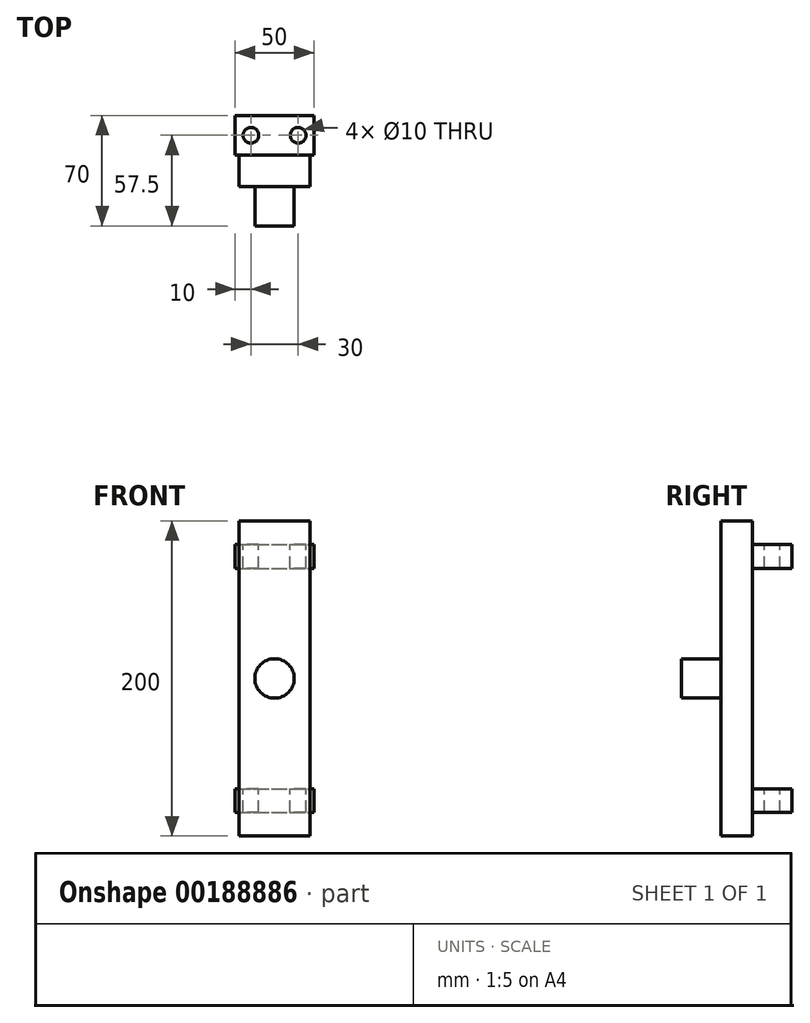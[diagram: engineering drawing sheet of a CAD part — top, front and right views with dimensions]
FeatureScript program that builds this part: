
annotation { "Feature Type Name" : "Feature", "Feature Type Description" : "" }
export const myFeature = defineFeature(function(context is Context, id is Id, definition is map)
    precondition{}
    {
        {
            var Q0;
            Q0=qCreatedBy(makeId("Front.planeOp"),FACE);
            var sketch = newSketch(context, id + "F0", { "sketchPlane" : qUnion([Q0])});
            skCircle(sketch, "E0", {"center": v(0, 0) * mm, "radius": 12.5 * mm});
            skSolve(sketch);
        }
        {
            var Q0;
            Q0 = qSketchRegion(id + "F0", true);
            extrude(context, id + "F1", {"entities" : qUnion([Q0]), "depth" : 45 * mm});
        }
        {
            var Q0;
            Q0=qCreatedBy(makeId("Front.planeOp"),FACE);
            cPlane(context, id + "F2", {"entities" : qUnion([Q0]), "cplaneType" : CPlaneType.OFFSET, "offset" : 20 * mm, "width" : 150 * mm, "height" : 150 * mm});
        }
        {
            var Q0;
            Q0=qCreatedBy(id+"F2.planeOp",FACE);
            var sketch = newSketch(context, id + "F3", { "sketchPlane" : qUnion([Q0])});
            skLineSegment(sketch, "E1.bottom", {"start": v(-22.5, -100) * mm, "end": v(22.5, -100) * mm});
            skLineSegment(sketch, "E1.top", {"start": v(-22.5, 100) * mm, "end": v(22.5, 100) * mm});
            skLineSegment(sketch, "E1.left", {"start": v(-22.5, -100) * mm, "end": v(-22.5, 100) * mm});
            skLineSegment(sketch, "E1.right", {"start": v(22.5, -100) * mm, "end": v(22.5, 100) * mm});
            skPoint(sketch, "E1.middle", {"position": v(0, 0) * mm});
            skSolve(sketch);
        }
        {
            var Q0;
            Q0 = qSketchRegion(id + "F3", true);
            extrude(context, id + "F4", {"entities" : qUnion([Q0]), "operationType" : NewBodyOperationType.ADD, "oppositeDirection" : true, "depth" : 20 * mm});
        }
        {
            var Q0;
            Q0=qCreatedBy(makeId("Front.planeOp"),FACE);
            cPlane(context, id + "F5", {"entities" : qUnion([Q0]), "cplaneType" : CPlaneType.OFFSET, "offset" : 25 * mm, "oppositeDirection" : true, "width" : 150 * mm, "height" : 150 * mm});
        }
        {
            var Q0;
            Q0=qCreatedBy(id+"F5.planeOp",FACE);
            var sketch = newSketch(context, id + "F6", { "sketchPlane" : qUnion([Q0])});
            skLineSegment(sketch, "E2.bottom", {"start": v(-25, 70) * mm, "end": v(25, 70) * mm});
            skLineSegment(sketch, "E2.top", {"start": v(-25, 85) * mm, "end": v(25, 85) * mm});
            skLineSegment(sketch, "E2.left", {"start": v(-25, 70) * mm, "end": v(-25, 85) * mm});
            skLineSegment(sketch, "E2.right", {"start": v(25, 70) * mm, "end": v(25, 85) * mm});
            skPoint(sketch, "E2.middle", {"position": v(0, 77.5) * mm});
            skLineSegment(sketch, "E3.bottom", {"start": v(-25, -85) * mm, "end": v(25, -85) * mm});
            skLineSegment(sketch, "E3.top", {"start": v(-25, -70) * mm, "end": v(25, -70) * mm});
            skLineSegment(sketch, "E3.left", {"start": v(-25, -85) * mm, "end": v(-25, -70) * mm});
            skLineSegment(sketch, "E3.right", {"start": v(25, -85) * mm, "end": v(25, -70) * mm});
            skPoint(sketch, "E3.middle", {"position": v(0, -77.5) * mm});
            skSolve(sketch);
        }
        {
            var Q0;
            Q0 = qSketchRegion(id + "F6", true);
            extrude(context, id + "F7", {"entities" : qUnion([Q0]), "operationType" : NewBodyOperationType.ADD, "depth" : 25 * mm});
        }
        {
            var Q0;
            Q0=makeQuery(id+"F7.opExtrude","SWEPT_FACE",FACE,{"disambiguationData":[OSD([sQuery(id+"F6.wireOp",EDGE,"E2.top")])]});
            var sketch = newSketch(context, id + "F8", { "sketchPlane" : qUnion([Q0])});
            skCircle(sketch, "E4", {"center": v(15, 12.5) * mm, "radius": 5 * mm});
            skCircle(sketch, "E5", {"center": v(-15, 12.5) * mm, "radius": 5 * mm});
            skSolve(sketch);
        }
        {
            var Q0;
            Q0 = qSketchRegion(id + "F8", true);
            extrude(context, id + "F9", {"entities" : qUnion([Q0]), "operationType" : NewBodyOperationType.REMOVE, "endBound" : BoundingType.THROUGH_ALL, "oppositeDirection" : true, "depth" : 25 * mm});
        }
    });
